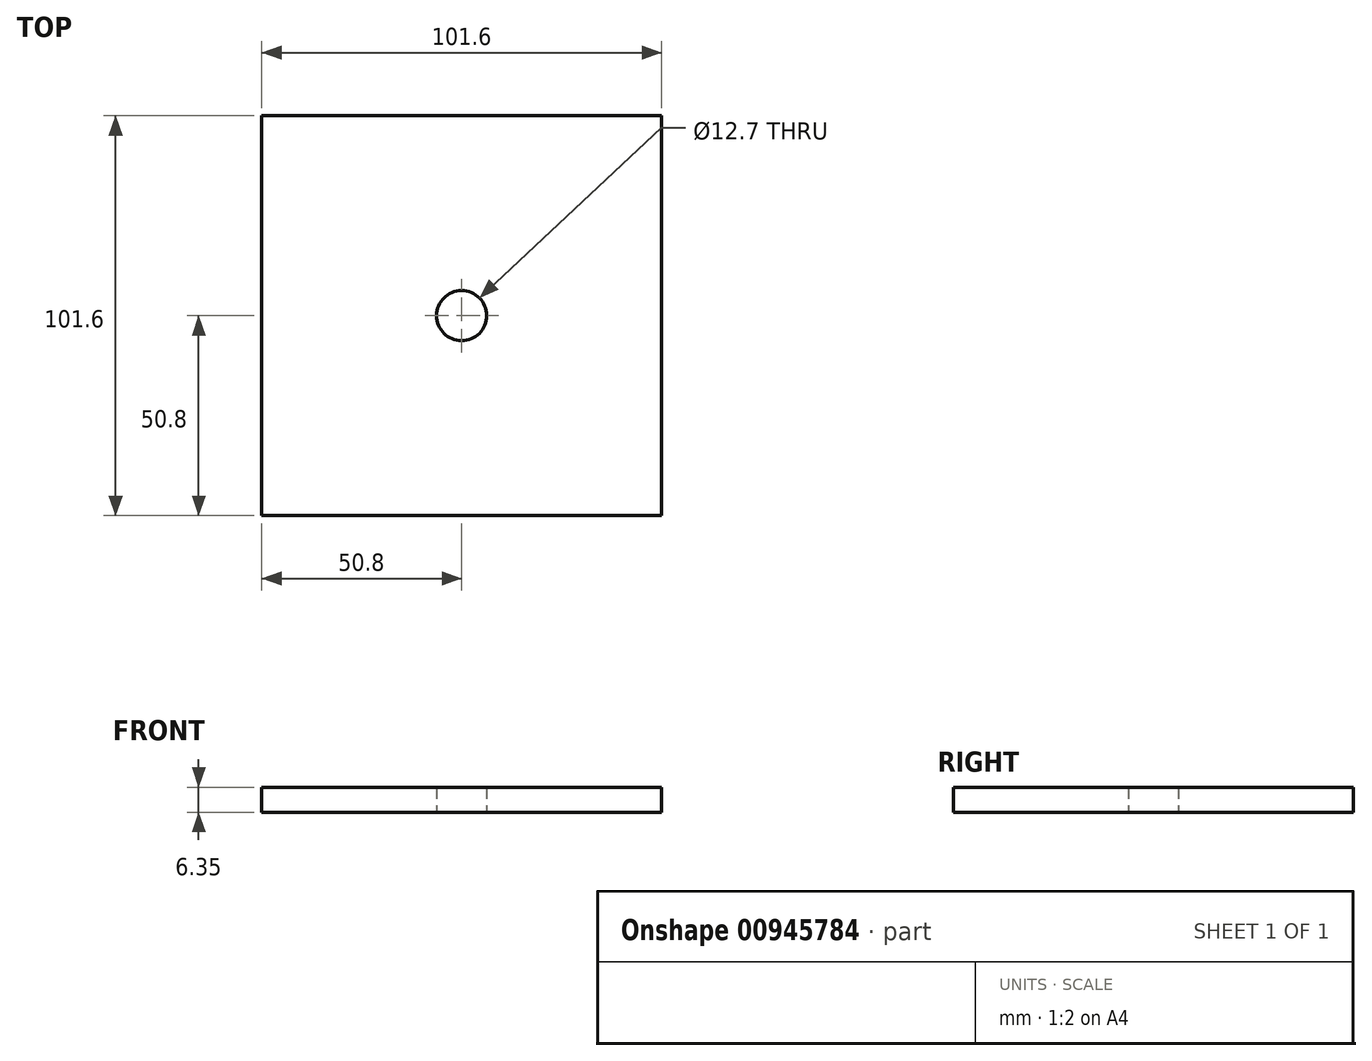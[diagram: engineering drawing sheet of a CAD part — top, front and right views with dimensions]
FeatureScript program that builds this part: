
annotation { "Feature Type Name" : "Feature", "Feature Type Description" : "" }
export const myFeature = defineFeature(function(context is Context, id is Id, definition is map)
    precondition{}
    {
        {
            var Q0;
            Q0=qCreatedBy(makeId("Top.planeOp"),FACE);
            var sketch = newSketch(context, id + "F0", { "sketchPlane" : qUnion([Q0])});
            skLineSegment(sketch, "E0.bottom", {"start": v(50.8, 50.8) * mm, "end": v(-50.8, 50.8) * mm});
            skLineSegment(sketch, "E0.top", {"start": v(50.8, -50.8) * mm, "end": v(-50.8, -50.8) * mm});
            skLineSegment(sketch, "E0.left", {"start": v(50.8, 50.8) * mm, "end": v(50.8, -50.8) * mm});
            skLineSegment(sketch, "E0.right", {"start": v(-50.8, 50.8) * mm, "end": v(-50.8, -50.8) * mm});
            skPoint(sketch, "E0.middle", {"position": v(0, 0) * mm});
            skCircle(sketch, "E1", {"center": v(0, 0) * mm, "radius": 6.35 * mm});
            skSolve(sketch);
        }
        {
            var Q0;
            Q0=qSketchRegion(id+"F0",true);
            extrude(context, id + "F1", {"entities" : qUnion([Q0]), "depth" : 6.35 * mm, "offsetDistance" : 25.4 * mm});
        }
    });
